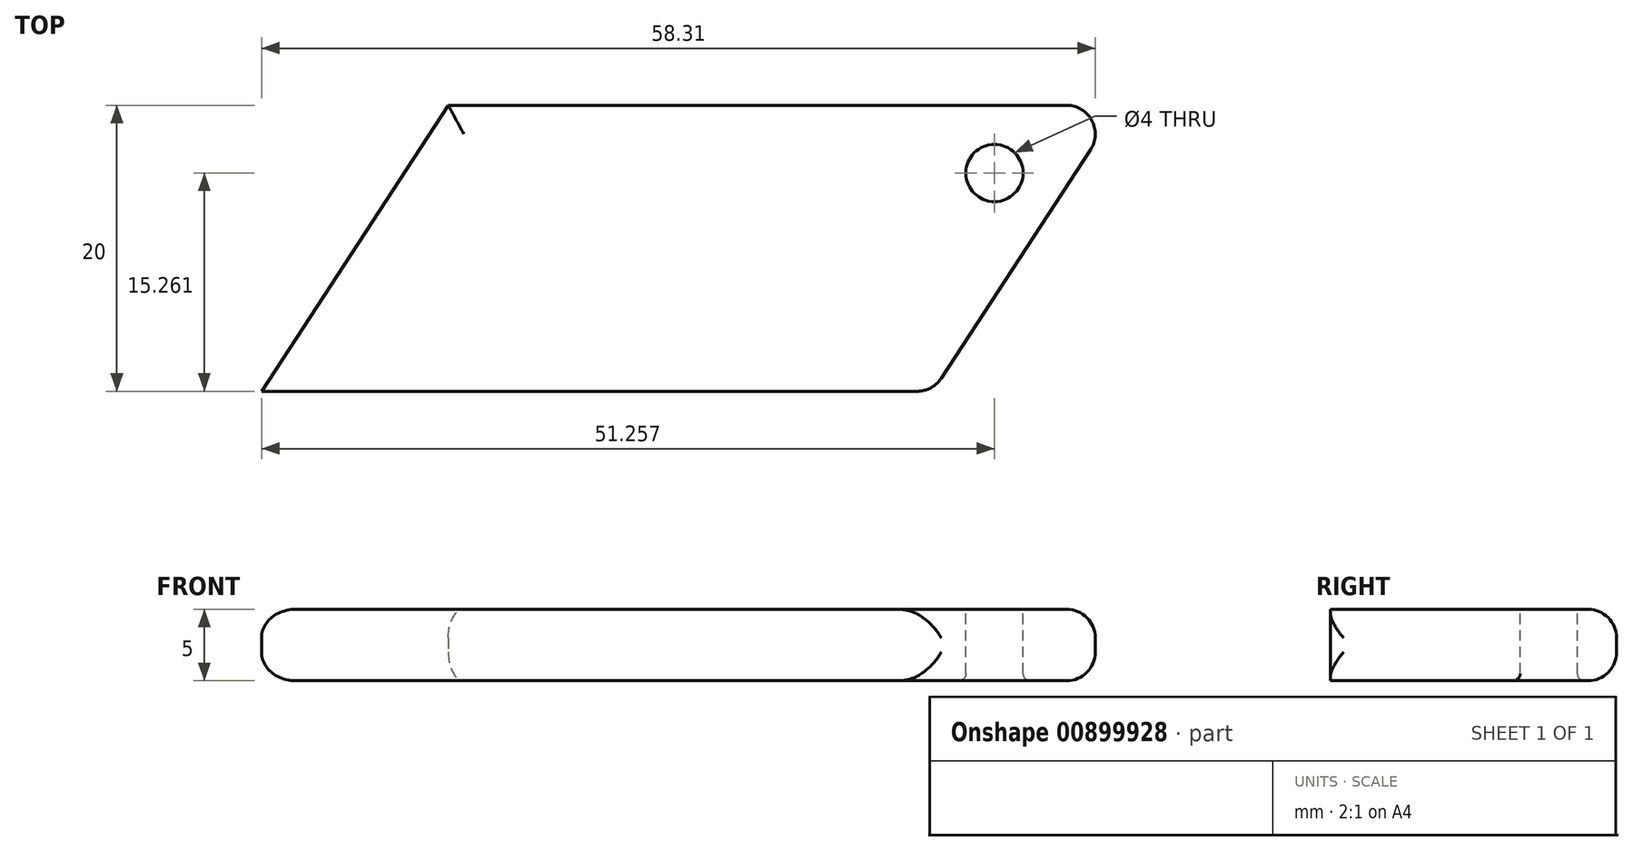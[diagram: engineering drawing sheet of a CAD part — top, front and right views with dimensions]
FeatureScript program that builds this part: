
annotation { "Feature Type Name" : "Feature", "Feature Type Description" : "" }
export const myFeature = defineFeature(function(context is Context, id is Id, definition is map)
    precondition{}
    {
        {
            var Q0;
            Q0=qCreatedBy(makeId("Top.planeOp"),FACE);
            var sketch = newSketch(context, id + "F0", { "sketchPlane" : qUnion([Q0])});
            skLineSegment(sketch, "E0.bottom", {"start": v(16.94, -10) * mm, "end": v(-30, -10) * mm});
            skLineSegment(sketch, "E0.top", {"start": v(30, 10) * mm, "end": v(-16.94, 10) * mm});
            skPoint(sketch, "E0.middle", {"position": v(0, 0) * mm});
            skLineSegment(sketch, "E1", {"start": v(-30, -10) * mm, "end": v(-16.94, 10) * mm});
            skLineSegment(sketch, "E2", {"start": v(30, 10) * mm, "end": v(16.94, -10) * mm});
            skPoint(sketch, "E0.right.end.orphan", {"position": v(-30, 10) * mm});
            skPoint(sketch, "E0.left.start.orphan", {"position": v(30, -10) * mm});
            skSolve(sketch);
        }
        {
            var Q0;
            Q0=makeQuery(id+"F0.imprint","IMPRINT",FACE,{"disambiguationData":[TD([[makeQuery(id+"F0.imprint","IMPRINT",EDGE,{"derivedFrom":sQuery(id+"F0.wireOp",EDGE,"E0.bottom")}),-1.0]])]});
            extrude(context, id + "F1", {"entities" : qUnion([Q0]), "depth" : 5 * mm, "offsetDistance" : 25.4 * mm});
        }
        {
            var Q0;
            Q0=makeQuery(id+"F1.opExtrude","CAP_EDGE",EDGE,{"disambiguationData":[OSD([sQuery(id+"F0.wireOp",EDGE,"E0.top")])],"isStart":false});
            var Q1;
            Q1=makeQuery(id+"F1.opExtrude","CAP_EDGE",EDGE,{"disambiguationData":[OSD([sQuery(id+"F0.wireOp",EDGE,"E1")])],"isStart":false});
            var Q2;
            Q2=makeQuery(id+"F1.opExtrude","CAP_EDGE",EDGE,{"disambiguationData":[OSD([sQuery(id+"F0.wireOp",EDGE,"E2")])],"isStart":false});
            var Q3;
            Q3=makeQuery(id+"F1.opExtrude","SWEPT_FACE",FACE,{"disambiguationData":[OSD([sQuery(id+"F0.wireOp",EDGE,"E2")])]});
            var Q4;
            Q4=makeQuery(id+"F1.opExtrude","CAP_EDGE",EDGE,{"disambiguationData":[OSD([sQuery(id+"F0.wireOp",EDGE,"E0.top")])],"isStart":true});
            var Q5;
            Q5=makeQuery(id+"F1.opExtrude","CAP_EDGE",EDGE,{"disambiguationData":[OSD([sQuery(id+"F0.wireOp",EDGE,"E1")])],"isStart":true});
            fillet(context, id + "F2", {"entities" : qUnion([Q0, Q1, Q2, Q3, Q4, Q5]), "radius" : 2 * mm, "tangentPropagation" : true, "allowEdgeOverflow" : false});
        }
        {
            var Q0;
            Q0=makeQuery(id+"F1.opExtrude","CAP_FACE",FACE,{"disambiguationData":[OSD([sQuery(id+"F0.wireOp",EDGE,"E0.bottom"),sQuery(id+"F0.wireOp",EDGE,"E0.top"),sQuery(id+"F0.wireOp",EDGE,"E1"),sQuery(id+"F0.wireOp",EDGE,"E2")])],"isStart":false});
            var sketch = newSketch(context, id + "F3", { "sketchPlane" : qUnion([Q0])});
            skCircle(sketch, "E3", {"center": v(21.26, 5.26) * mm, "radius": 2 * mm});
            skSolve(sketch);
        }
        {
            var Q0;
            Q0=makeQuery(id+"F3.imprint","IMPRINT",FACE,{"disambiguationData":[TD([[makeQuery(id+"F3.imprint","IMPRINT",EDGE,{"derivedFrom":sQuery(id+"F3.wireOp",EDGE,"E3")}),1.0]])]});
            extrude(context, id + "F4", {"entities" : qUnion([Q0]), "operationType" : NewBodyOperationType.REMOVE, "oppositeDirection" : true, "depth" : 25.4 * mm, "offsetDistance" : 25.4 * mm});
        }
        {
            var Q0;
            Q0=makeQuery(id+"F4.boolean.opBoolean","COPY",EDGE,{"derivedFrom":makeQuery(id+"F4.opExtrude","CAP_EDGE",EDGE,{"disambiguationData":[OSD([sQuery(id+"F3.wireOp",EDGE,"E3")])],"isStart":true})});
            var Q1;
            Q1=makeQuery(id+"F4.boolean.opBoolean","INTERSECT",EDGE,{"derivedFrom":[makeQuery(id+"F1.opExtrude","CAP_FACE",FACE,{"disambiguationData":[OSD([sQuery(id+"F0.wireOp",EDGE,"E0.bottom"),sQuery(id+"F0.wireOp",EDGE,"E0.top"),sQuery(id+"F0.wireOp",EDGE,"E1"),sQuery(id+"F0.wireOp",EDGE,"E2")])],"isStart":true}),makeQuery(id+"F4.opExtrude","SWEPT_FACE",FACE,{"disambiguationData":[OSD([sQuery(id+"F3.wireOp",EDGE,"E3")])]})]});
            fillet(context, id + "F5", {"entities" : qUnion([Q0, Q1]), "radius" : 0.5 * mm, "tangentPropagation" : true, "allowEdgeOverflow" : false});
        }
    });
